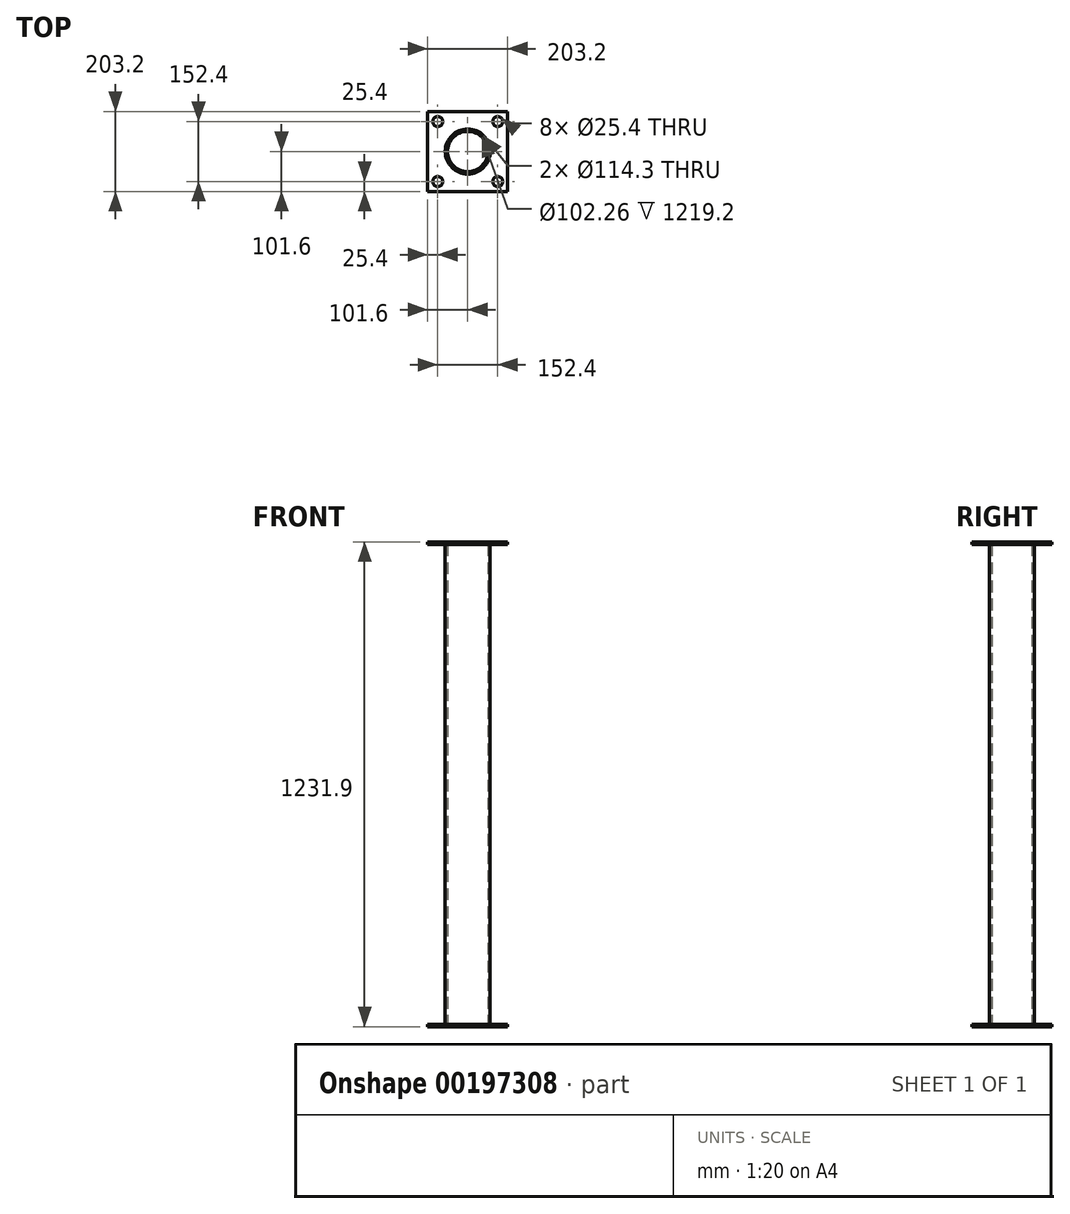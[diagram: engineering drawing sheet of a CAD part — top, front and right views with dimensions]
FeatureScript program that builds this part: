
annotation { "Feature Type Name" : "Feature", "Feature Type Description" : "" }
export const myFeature = defineFeature(function(context is Context, id is Id, definition is map)
    precondition{}
    {
        {
            var Q0;
            Q0=qCreatedBy(makeId("Top.planeOp"),FACE);
            var sketch = newSketch(context, id + "F0", { "sketchPlane" : qUnion([Q0])});
            skCircle(sketch, "E0", {"center": v(0, 0) * mm, "radius": 57.15 * mm});
            skCircle(sketch, "E1.0", {"center": v(0, 0) * mm, "radius": 51.13 * mm});
            skSolve(sketch);
        }
        {
            var Q0;
            Q0=qSketchRegion(id+"F0",true);
            extrude(context, id + "F1", {"entities" : qUnion([Q0]), "endBound" : BoundingType.SYMMETRIC, "depth" : 1219.2 * mm});
        }
        {
            var Q0;
            Q0=makeQuery(id+"F1.opExtrude","CAP_FACE",FACE,{"disambiguationData":[OSD([sQuery(id+"F0.wireOp",EDGE,"E0"),sQuery(id+"F0.wireOp",EDGE,"E1.0")])],"isStart":false});
            var sketch = newSketch(context, id + "F2", { "sketchPlane" : qUnion([Q0])});
            skLineSegment(sketch, "E2.bottom", {"start": v(101.6, -101.6) * mm, "end": v(-101.6, -101.6) * mm});
            skLineSegment(sketch, "E2.top", {"start": v(101.6, 101.6) * mm, "end": v(-101.6, 101.6) * mm});
            skLineSegment(sketch, "E2.left", {"start": v(101.6, -101.6) * mm, "end": v(101.6, 101.6) * mm});
            skLineSegment(sketch, "E2.right", {"start": v(-101.6, -101.6) * mm, "end": v(-101.6, 101.6) * mm});
            skPoint(sketch, "E2.middle", {"position": v(0, 0) * mm});
            skSolve(sketch);
        }
        {
            var Q0;
            Q0=makeQuery(id+"F2.imprint","IMPRINT",FACE,{"disambiguationData":[TD([[makeQuery(id+"F2.imprint","IMPRINT",EDGE,{"derivedFrom":sQuery(id+"F2.wireOp",EDGE,"E2.bottom")}),-1.0]])]});
            extrude(context, id + "F3", {"entities" : qUnion([Q0]), "depth" : 6.35 * mm});
        }
        {
            var Q0;
            Q0=makeQuery(id+"F3.opExtrude","CAP_FACE",FACE,{"disambiguationData":[OSD([sQuery(id+"F0.wireOp",EDGE,"E0"),sQuery(id+"F2.wireOp",EDGE,"E2.bottom"),sQuery(id+"F2.wireOp",EDGE,"E2.top"),sQuery(id+"F2.wireOp",EDGE,"E2.left"),sQuery(id+"F2.wireOp",EDGE,"E2.right")])],"isStart":false});
            var sketch = newSketch(context, id + "F4", { "sketchPlane" : qUnion([Q0])});
            skLineSegment(sketch, "E3.bottom", {"start": v(76.2, -76.2) * mm, "end": v(-76.2, -76.2) * mm, "construction": true});
            skLineSegment(sketch, "E3.top", {"start": v(76.2, 76.2) * mm, "end": v(-76.2, 76.2) * mm, "construction": true});
            skLineSegment(sketch, "E3.left", {"start": v(76.2, -76.2) * mm, "end": v(76.2, 76.2) * mm, "construction": true});
            skLineSegment(sketch, "E3.right", {"start": v(-76.2, -76.2) * mm, "end": v(-76.2, 76.2) * mm, "construction": true});
            skPoint(sketch, "E3.middle", {"position": v(0, 0) * mm});
            skCircle(sketch, "E4", {"center": v(-76.2, 76.2) * mm, "radius": 12.7 * mm});
            skCircle(sketch, "E5", {"center": v(76.2, 76.2) * mm, "radius": 12.7 * mm});
            skCircle(sketch, "E6", {"center": v(-76.2, -76.2) * mm, "radius": 12.7 * mm});
            skCircle(sketch, "E7", {"center": v(76.2, -76.2) * mm, "radius": 12.7 * mm});
            skSolve(sketch);
        }
        {
            var Q0;
            Q0=qSketchRegion(id+"F4",true);
            var Q1;
            Q1=makeQuery(id+"F3.opExtrude","CAP_FACE",FACE,{"disambiguationData":[OSD([sQuery(id+"F0.wireOp",EDGE,"E0"),sQuery(id+"F2.wireOp",EDGE,"E2.bottom"),sQuery(id+"F2.wireOp",EDGE,"E2.top"),sQuery(id+"F2.wireOp",EDGE,"E2.left"),sQuery(id+"F2.wireOp",EDGE,"E2.right")])],"isStart":true});
            extrude(context, id + "F5", {"entities" : qUnion([Q0]), "operationType" : NewBodyOperationType.REMOVE, "endBound" : BoundingType.UP_TO_SURFACE, "oppositeDirection" : true, "endBoundEntityFace" : qUnion([Q1]), "depth" : 25.4 * mm});
        }
        {
            var Q0;
            Q0=makeQuery(id+"F3.opExtrude","SWEPT_BODY",BODY,{"disambiguationData":[OSD([sQuery(id+"F0.wireOp",EDGE,"E0"),sQuery(id+"F2.wireOp",EDGE,"E2.bottom"),sQuery(id+"F2.wireOp",EDGE,"E2.top"),sQuery(id+"F2.wireOp",EDGE,"E2.left"),sQuery(id+"F2.wireOp",EDGE,"E2.right")])]});
            var Q1;
            Q1=qCreatedBy(makeId("Top.planeOp"),FACE);
            mirror(context, id + "F6", {"entities" : qUnion([Q0]), "mirrorPlane" : qUnion([Q1])});
        }
    });
